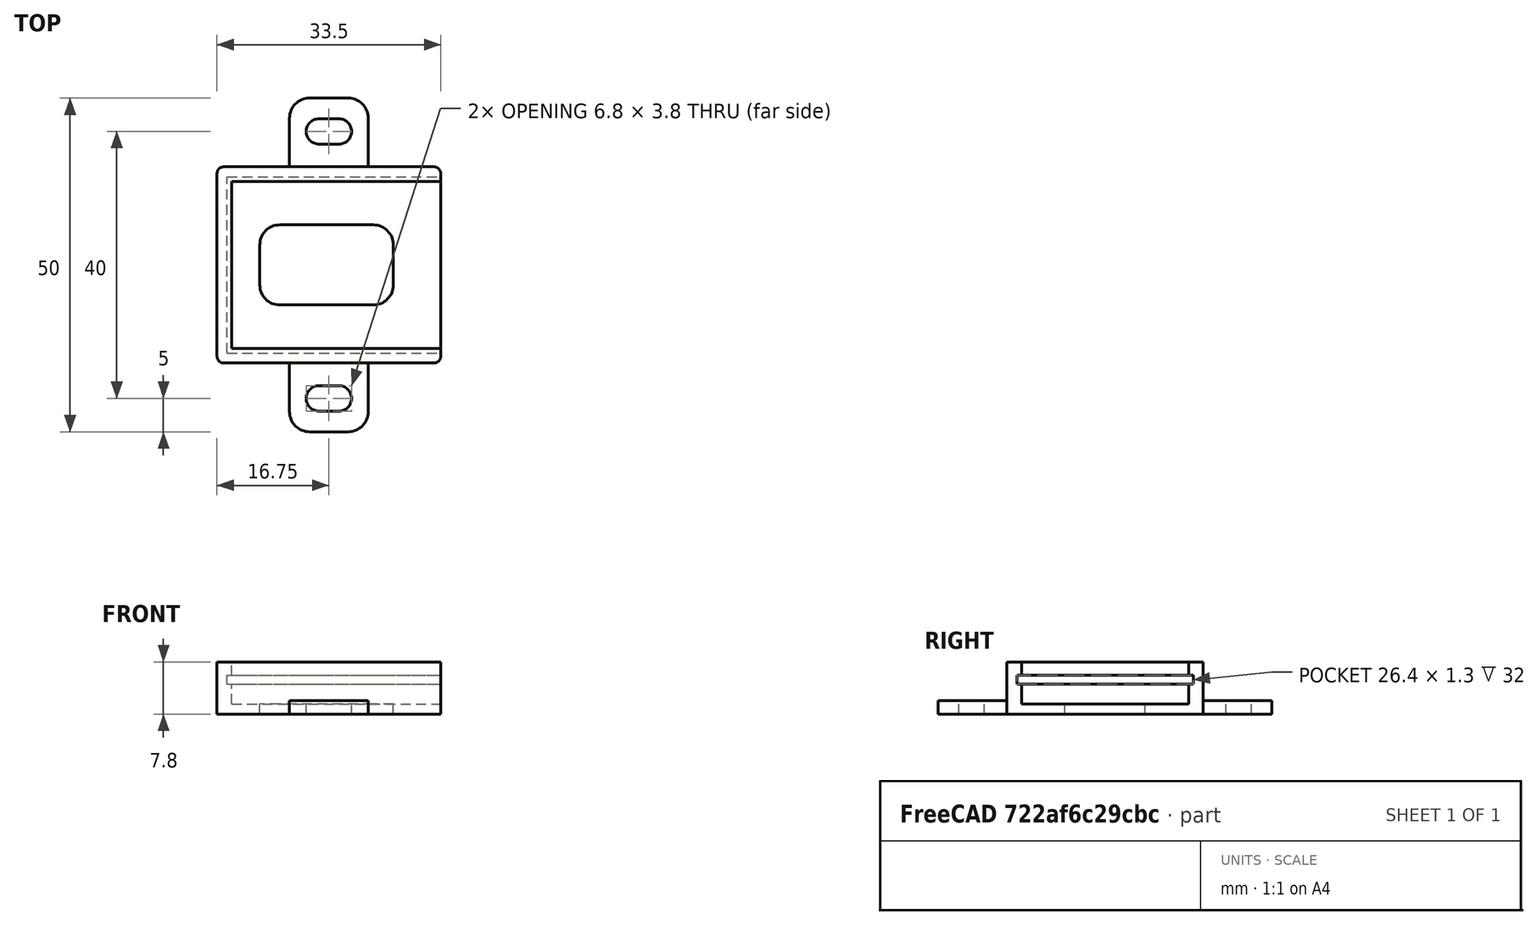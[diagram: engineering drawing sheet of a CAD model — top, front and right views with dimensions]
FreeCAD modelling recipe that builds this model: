
FCSTD DOCUMENT  (FreeCAD 0.19R)
Label: picaxe8m2_battcut
License: FreeArt
LicenseURL: http://artlibre.org/licence/lal
objects: Part::Box×4, Part::Fillet×2, Part::MultiFuse×2, Spreadsheet::Sheet×1, Part::Feature×1, Part::Cut×1, App::Part×1
note: 10 computed .brp shape members not serialized (recipe doc carries the construction recipe); baked Part::Feature solids carry a one-line shape summary decoded from their .brp

FEATURE [Spreadsheet::Sheet] Spreadsheet  label="p"
  cells = A1=pcb_x; B1(pcb_x)=32; A2=pcb_y; B2(pcb_y)=26.4; A3=pcb_z; B3(pcb_z)=1.3; A4=pcb_under; B4(pcb_under)=3; A5=side_wall; B5(side_wall)=1.5; A6=pcb_side_lane; B6(pcb_side_lane)=0.7; A7=bottom_wall; B7(bottom_wall)=1.5; A8=pcb_above; B8(pcb_above)=2; A9=bottom_hole_x; B9(bottom_hole_x)=20; A10=bottom_hole_y; B10(bottom_hole_y)=12
FEATURE [Part::Box] Box  label="external cube"
  AttacherType = Attacher::AttachEngine3D
  Height = 7.8
  Length = 33.5
  Width = 29.4
  expr: Length = <<p>>.pcb_x + <<p>>.side_wall
  expr: Width = <<p>>.pcb_y + 2 * <<p>>.side_wall
  expr: Height = <<p>>.bottom_wall + <<p>>.pcb_under + <<p>>.pcb_z + <<p>>.pcb_above
FEATURE [Part::Box] Box006  label="internal cube"
  AttacherType = Attacher::AttachEngine3D
  Height = 6.3
  Length = 32.1
  Placement = pos=(2.2,2.2,1.5) rot=(0,0,1;0rad)
  Width = 25
  expr: Length = <<p>>.pcb_x - 2 * <<p>>.pcb_side_lane + <<p>>.side_wall
  expr: Width = <<p>>.pcb_y - 2 * <<p>>.pcb_side_lane
  expr: Height = <<p>>.pcb_under + <<p>>.pcb_z + <<p>>.pcb_above
  expr: .Placement.Base.z = <<p>>.bottom_wall
  expr: .Placement.Base.x = <<p>>.side_wall + <<p>>.pcb_side_lane
  expr: .Placement.Base.y = <<p>>.side_wall + <<p>>.pcb_side_lane
FEATURE [Part::Box] Box007  label="pcb extract cube"
  AttacherType = Attacher::AttachEngine3D
  Height = 1.3
  Length = 32
  Placement = pos=(1.5,1.5,4.5) rot=(0,0,1;0rad)
  Width = 26.4
  expr: Height = <<p>>.pcb_z
  expr: .Placement.Base.z = <<p>>.bottom_wall + <<p>>.pcb_under
  expr: Width = <<p>>.pcb_y
  expr: Length = <<p>>.pcb_x
  expr: .Placement.Base.x = <<p>>.side_wall
  expr: .Placement.Base.y = <<p>>.side_wall
FEATURE [Part::Fillet] Fillet  label="external fillet"
  Base = -> Box
  Edges = 4 edges r=1: [Edge1,Edge3,Edge5,Edge7]
FEATURE [Part::Box] Box008  label="bottom hole"
  AttacherType = Attacher::AttachEngine3D
  Height = 10
  Length = 20
  Placement = pos=(6.4,8.7,0) rot=(0,0,1;0rad)
  Width = 12
  expr: .Placement.Base.y = (<<p>>.pcb_y + 2 * <<p>>.side_wall - <<p>>.bottom_hole_y) / 2
  expr: .Placement.Base.x = (<<p>>.pcb_x + <<p>>.side_wall - <<p>>.pcb_side_lane - <<p>>.bottom_hole_x) / 2
  expr: Width = <<p>>.bottom_hole_y
  expr: Length = <<p>>.bottom_hole_x
FEATURE [Part::Fillet] Fillet001  label="bottom hole fillet"
  Base = -> Box008
  Edges = 4 edges r=3: [Edge1,Edge3,Edge5,Edge7]
FEATURE [Part::MultiFuse] Fusion  label="extract fusion"
  Shapes = -> [Box006,Box007,Fillet001]
FEATURE [Part::Feature] Cut002001  label="attach plane y dir001"
  Placement = pos=(10.85,-10.3,0) rot=(0,0,1;0rad)
  shape: bbox 11.8 x 50 x 2 mm, 20 faces (baked)
FEATURE [Part::MultiFuse] Fusion001  label="solid fusion"
  Shapes = -> [Fillet,Cut002001]
FEATURE [Part::Cut] Cut  label="body cut"
  Base = -> Fusion001
  Tool = -> Fusion
FEATURE [App::Part] Part  label="pcb box part"
  Group = -> [Box,Fillet,Fusion001,Fusion,Box007,Box006,Cut]
  Origin = -> Origin
